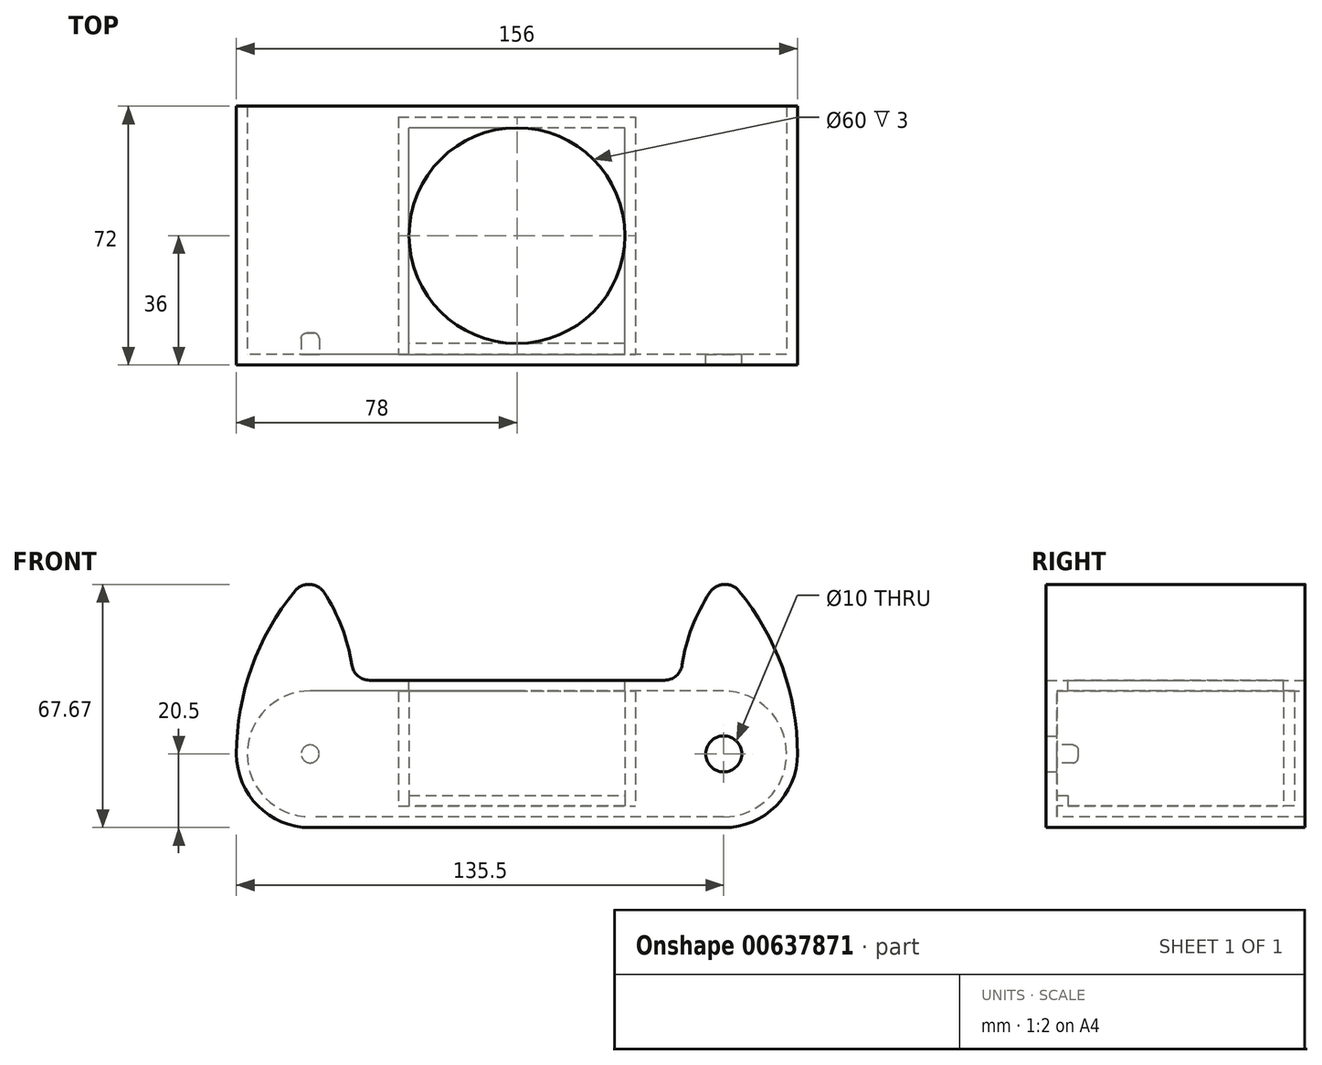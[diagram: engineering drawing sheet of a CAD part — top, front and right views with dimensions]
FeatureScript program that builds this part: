
annotation { "Feature Type Name" : "Feature", "Feature Type Description" : "" }
export const myFeature = defineFeature(function(context is Context, id is Id, definition is map)
    precondition{}
    {
        {
            var Q0;
            Q0=qCreatedBy(makeId("Front.planeOp"),FACE);
            var sketch = newSketch(context, id + "F0", { "sketchPlane" : qUnion([Q0])});
            skLineSegment(sketch, "E0.bottom", {"start": v(57.5, 17.5) * mm, "end": v(-57.5, 17.5) * mm});
            skLineSegment(sketch, "E0.top", {"start": v(57.5, -17.5) * mm, "end": v(-57.5, -17.5) * mm});
            skPoint(sketch, "E0.middle", {"position": v(0, 0) * mm});
            skArc(sketch, "E1", {"start": v(-57.5, 17.5) * mm, "mid": v(-75, 0) * mm, "end": v(-57.5, -17.5) * mm});
            skArc(sketch, "E2", {"start": v(57.5, -17.5) * mm, "mid": v(75, 0) * mm, "end": v(57.5, 17.5) * mm});
            skCircle(sketch, "E3", {"center": v(57.5, 0) * mm, "radius": 5 * mm});
            skSolve(sketch);
        }
        {
            var Q0;
            Q0 = qSketchRegion(id + "F0", true);
            extrude(context, id + "F1", {"entities" : qUnion([Q0]), "depth" : 3 * mm, "offsetDistance" : 25 * mm});
        }
        {
            var Q0;
            Q0=makeQuery(id+"F1.opExtrude","CAP_FACE",FACE,{"disambiguationData":[OSD([sQuery(id+"F0.wireOp",EDGE,"E0.bottom"),sQuery(id+"F0.wireOp",EDGE,"E0.top"),sQuery(id+"F0.wireOp",EDGE,"E1"),sQuery(id+"F0.wireOp",EDGE,"E2"),sQuery(id+"F0.wireOp",EDGE,"E3")])],"isStart":true});
            var sketch = newSketch(context, id + "F2", { "sketchPlane" : qUnion([Q0])});
            skLineSegment(sketch, "E4.bottom", {"start": v(33, -11.5) * mm, "end": v(-33, -11.5) * mm});
            skLineSegment(sketch, "E4.top", {"start": v(33, -14.5) * mm, "end": v(-33, -14.5) * mm});
            skLineSegment(sketch, "E4.left", {"start": v(33, -11.5) * mm, "end": v(33, -14.5) * mm});
            skLineSegment(sketch, "E4.right", {"start": v(-33, -11.5) * mm, "end": v(-33, -14.5) * mm});
            skPoint(sketch, "E4.middle", {"position": v(0, -13) * mm});
            skSolve(sketch);
        }
        {
            var Q0;
            Q0 = qSketchRegion(id + "F2", true);
            extrude(context, id + "F3", {"entities" : qUnion([Q0]), "operationType" : NewBodyOperationType.ADD, "depth" : 66 * mm, "offsetDistance" : 25 * mm});
        }
        {
            var Q0;
            Q0=makeQuery(id+"F3.opExtrude","SWEPT_FACE",FACE,{"disambiguationData":[OSD([sQuery(id+"F2.wireOp",EDGE,"E4.top")])]});
            var sketch = newSketch(context, id + "F4", { "sketchPlane" : qUnion([Q0])});
            skLineSegment(sketch, "E5", {"start": v(0, 0) * mm, "end": v(0, -66) * mm, "construction": true});
            skLineSegment(sketch, "E6.bottom", {"start": v(30, -3) * mm, "end": v(-30, -3) * mm});
            skLineSegment(sketch, "E6.top", {"start": v(30, -63) * mm, "end": v(-30, -63) * mm});
            skLineSegment(sketch, "E6.left", {"start": v(30, -3) * mm, "end": v(30, -63) * mm});
            skLineSegment(sketch, "E6.right", {"start": v(-30, -3) * mm, "end": v(-30, -63) * mm});
            skPoint(sketch, "E6.middle", {"position": v(0, -33) * mm});
            skSolve(sketch);
        }
        {
            var Q0;
            Q0 = qSketchRegion(id + "F4", true);
            extrude(context, id + "F5", {"entities" : qUnion([Q0]), "operationType" : NewBodyOperationType.REMOVE, "oppositeDirection" : true, "depth" : 25 * mm, "offsetDistance" : 25 * mm});
        }
        {
            var Q0;
            Q0=makeQuery(id+"F1.opExtrude","CAP_FACE",FACE,{"disambiguationData":[OSD([sQuery(id+"F0.wireOp",EDGE,"E0.bottom"),sQuery(id+"F0.wireOp",EDGE,"E0.top"),sQuery(id+"F0.wireOp",EDGE,"E1"),sQuery(id+"F0.wireOp",EDGE,"E2"),sQuery(id+"F0.wireOp",EDGE,"E3")])],"isStart":true});
            var sketch = newSketch(context, id + "F6", { "sketchPlane" : qUnion([Q0])});
            skLineSegment(sketch, "E7", {"start": v(57.5, 17.5) * mm, "end": v(57.5, -17.5) * mm, "construction": true});
            skCircle(sketch, "E8", {"center": v(57.5, 0) * mm, "radius": 2.5 * mm});
            skSolve(sketch);
        }
        {
            var Q0;
            Q0 = qSketchRegion(id + "F6", true);
            extrude(context, id + "F7", {"entities" : qUnion([Q0]), "operationType" : NewBodyOperationType.ADD, "depth" : 5.9 * mm, "offsetDistance" : 25 * mm});
        }
        {
            var Q0;
            Q0=makeQuery(id+"F7.opExtrude","CAP_EDGE",EDGE,{"disambiguationData":[OSD([sQuery(id+"F6.wireOp",EDGE,"E8")])],"isStart":false});
            fillet(context, id + "F8", {"entities" : qUnion([Q0]), "radius" : 1.5 * mm, "tangentPropagation" : true, "allowEdgeOverflow" : false});
        }
        {
            var Q0;
            Q0=makeQuery(id+"F1.opExtrude","CAP_FACE",FACE,{"disambiguationData":[OSD([sQuery(id+"F0.wireOp",EDGE,"E0.bottom"),sQuery(id+"F0.wireOp",EDGE,"E0.top"),sQuery(id+"F0.wireOp",EDGE,"E1"),sQuery(id+"F0.wireOp",EDGE,"E2"),sQuery(id+"F0.wireOp",EDGE,"E3")])],"isStart":true});
            var sketch = newSketch(context, id + "F9", { "sketchPlane" : qUnion([Q0])});
            skLineSegment(sketch, "E9", {"start": v(75, 0) * mm, "end": v(78, 0) * mm});
            skLineSegment(sketch, "E10", {"start": v(-75, 0) * mm, "end": v(-78, 0) * mm});
            skLineSegment(sketch, "E11", {"start": v(-57.5, -17.5) * mm, "end": v(-57.5, -20.5) * mm});
            skLineSegment(sketch, "E12", {"start": v(57.5, -17.5) * mm, "end": v(57.5, -20.5) * mm});
            skArc(sketch, "E13", {"start": v(-75, 0) * mm, "mid": v(-69.87, -12.37) * mm, "end": v(-57.5, -17.5) * mm});
            skArc(sketch, "E14", {"start": v(57.5, -17.5) * mm, "mid": v(69.87, -12.37) * mm, "end": v(75, 0) * mm});
            skArc(sketch, "E15", {"start": v(57.5, -20.5) * mm, "mid": v(72, -14.5) * mm, "end": v(78, 0) * mm});
            skArc(sketch, "E16", {"start": v(-78, 0) * mm, "mid": v(-72, -14.5) * mm, "end": v(-57.5, -20.5) * mm});
            skLineSegment(sketch, "E17", {"start": v(-57.5, -20.5) * mm, "end": v(57.5, -20.5) * mm});
            skLineSegment(sketch, "E18", {"start": v(57.5, -17.5) * mm, "end": v(-57.5, -17.5) * mm});
            skSolve(sketch);
        }
        {
            var Q0;
            Q0 = qSketchRegion(id + "F9", true);
            extrude(context, id + "F10", {"entities" : qUnion([Q0]), "operationType" : NewBodyOperationType.ADD, "depth" : 69 * mm, "offsetDistance" : 25 * mm, "hasSecondDirection" : true, "secondDirectionOppositeDirection" : true, "secondDirectionDepth" : 3 * mm});
        }
        {
            var Q0;
            Q0=makeQuery(id+"F3.opExtrude","SWEPT_FACE",FACE,{"disambiguationData":[OSD([sQuery(id+"F2.wireOp",EDGE,"E4.bottom")])]});
            var sketch = newSketch(context, id + "F11", { "sketchPlane" : qUnion([Q0])});
            skLineSegment(sketch, "E19.bottom", {"start": v(-33, 66) * mm, "end": v(33, 66) * mm});
            skLineSegment(sketch, "E19.top", {"start": v(-33, 63) * mm, "end": v(33, 63) * mm});
            skLineSegment(sketch, "E19.left", {"start": v(-33, 66) * mm, "end": v(-33, 63) * mm});
            skLineSegment(sketch, "E19.right", {"start": v(33, 66) * mm, "end": v(33, 63) * mm});
            skSolve(sketch);
        }
        {
            var Q0;
            Q0 = qSketchRegion(id + "F11", true);
            extrude(context, id + "F12", {"entities" : qUnion([Q0]), "operationType" : NewBodyOperationType.ADD, "depth" : 29 * mm, "offsetDistance" : 25 * mm});
        }
        {
            var Q0;
            Q0=makeQuery(id+"F3.opExtrude","SWEPT_FACE",FACE,{"disambiguationData":[OSD([sQuery(id+"F2.wireOp",EDGE,"E4.bottom")])]});
            var sketch = newSketch(context, id + "F13", { "sketchPlane" : qUnion([Q0])});
            skLineSegment(sketch, "E20.bottom", {"start": v(-33, 0) * mm, "end": v(-30, 0) * mm});
            skLineSegment(sketch, "E20.top", {"start": v(-33, 63) * mm, "end": v(-30, 63) * mm});
            skLineSegment(sketch, "E20.left", {"start": v(-33, 0) * mm, "end": v(-33, 63) * mm});
            skLineSegment(sketch, "E20.right", {"start": v(-30, 0) * mm, "end": v(-30, 63) * mm});
            skLineSegment(sketch, "E21.bottom", {"start": v(33, 0) * mm, "end": v(30, 0) * mm});
            skLineSegment(sketch, "E21.top", {"start": v(33, 63) * mm, "end": v(30, 63) * mm});
            skLineSegment(sketch, "E21.left", {"start": v(33, 0) * mm, "end": v(33, 63) * mm});
            skLineSegment(sketch, "E21.right", {"start": v(30, 0) * mm, "end": v(30, 63) * mm});
            skSolve(sketch);
        }
        {
            var Q0;
            Q0 = qSketchRegion(id + "F13", true);
            extrude(context, id + "F14", {"entities" : qUnion([Q0]), "operationType" : NewBodyOperationType.ADD, "depth" : 29 * mm, "offsetDistance" : 25 * mm});
        }
        {
            var Q0;
            Q0=makeQuery(id+"F10.opExtrude","CAP_FACE",FACE,{"disambiguationData":[OSD([sQuery(id+"F9.wireOp",EDGE,"E9"),sQuery(id+"F9.wireOp",EDGE,"E10"),sQuery(id+"F9.wireOp",EDGE,"E13"),sQuery(id+"F9.wireOp",EDGE,"E14"),sQuery(id+"F9.wireOp",EDGE,"E15"),sQuery(id+"F9.wireOp",EDGE,"E16"),sQuery(id+"F9.wireOp",EDGE,"E17"),sQuery(id+"F9.wireOp",EDGE,"E18")])],"isStart":false});
            var sketch = newSketch(context, id + "F15", { "sketchPlane" : qUnion([Q0])});
            skLineSegment(sketch, "E22.bottom", {"start": v(57.5, 17.5) * mm, "end": v(-57.5, 17.5) * mm, "construction": true});
            skLineSegment(sketch, "E22.top", {"start": v(57.5, 17.5) * mm, "end": v(-57.5, 17.5) * mm, "construction": true});
            skLineSegment(sketch, "E22.left", {"start": v(57.5, 17.5) * mm, "end": v(57.5, 17.5) * mm});
            skLineSegment(sketch, "E22.right", {"start": v(-57.5, 17.5) * mm, "end": v(-57.5, 17.5) * mm});
            skPoint(sketch, "E22.middle", {"position": v(0, 17.5) * mm});
            skArc(sketch, "E23", {"start": v(-57.5, 17.5) * mm, "mid": v(-69.87, 12.37) * mm, "end": v(-75, 0) * mm});
            skArc(sketch, "E24", {"start": v(75, 0) * mm, "mid": v(69.87, 12.37) * mm, "end": v(57.5, 17.5) * mm});
            skLineSegment(sketch, "E25", {"start": v(-57.5, 17.5) * mm, "end": v(57.5, 17.5) * mm});
            skLineSegment(sketch, "E26.bottom", {"start": v(-78, 0) * mm, "end": v(-45.5, 0) * mm, "construction": true});
            skLineSegment(sketch, "E26.top", {"start": v(-78, 50) * mm, "end": v(-45.5, 50) * mm, "construction": true});
            skLineSegment(sketch, "E26.left", {"start": v(-78, 0) * mm, "end": v(-78, 50) * mm, "construction": true});
            skLineSegment(sketch, "E26.right", {"start": v(-45.5, 0) * mm, "end": v(-45.5, 50) * mm, "construction": true});
            skLineSegment(sketch, "E27.bottom", {"start": v(78, 0) * mm, "end": v(45.5, 0) * mm, "construction": true});
            skLineSegment(sketch, "E27.top", {"start": v(78, 50) * mm, "end": v(45.5, 50) * mm, "construction": true});
            skLineSegment(sketch, "E27.left", {"start": v(78, 0) * mm, "end": v(78, 50) * mm, "construction": true});
            skLineSegment(sketch, "E27.right", {"start": v(45.5, 0) * mm, "end": v(45.5, 50) * mm, "construction": true});
            skLineSegment(sketch, "E28", {"start": v(-45.5, 20.5) * mm, "end": v(45.5, 20.5) * mm});
            skPoint(sketch, "E28.endSnap0", {"position": v(45.5, 25) * mm});
            skArc(sketch, "E29", {"start": v(-57.5, 50) * mm, "mid": v(-72.68, 27.02) * mm, "end": v(-78, 0) * mm});
            skArc(sketch, "E30", {"start": v(-45.5, 20.5) * mm, "mid": v(-49.09, 36.23) * mm, "end": v(-57.5, 50) * mm});
            skArc(sketch, "E31", {"start": v(78, 0) * mm, "mid": v(72.68, 27.02) * mm, "end": v(57.5, 50) * mm});
            skArc(sketch, "E32", {"start": v(57.5, 50) * mm, "mid": v(49.09, 36.23) * mm, "end": v(45.5, 20.5) * mm});
            skLineSegment(sketch, "E33", {"start": v(78, 0) * mm, "end": v(75, 0) * mm});
            skLineSegment(sketch, "E34", {"start": v(-75, 0) * mm, "end": v(-78, 0) * mm});
            skSolve(sketch);
        }
        {
            var Q0;
            Q0 = qSketchRegion(id + "F15", true);
            extrude(context, id + "F16", {"entities" : qUnion([Q0]), "operationType" : NewBodyOperationType.ADD, "oppositeDirection" : true, "depth" : 72 * mm, "offsetDistance" : 25 * mm});
        }
        {
            var Q0;
            Q0=makeQuery(id+"F16.opExtrude","SWEPT_EDGE",EDGE,{"disambiguationData":[OSD([sQuery(id+"F15.wireOp",EDGE,"E29"),sQuery(id+"F15.wireOp",EDGE,"E30")])]});
            var Q1;
            Q1=makeQuery(id+"F16.opExtrude","SWEPT_EDGE",EDGE,{"disambiguationData":[OSD([sQuery(id+"F15.wireOp",EDGE,"E31"),sQuery(id+"F15.wireOp",EDGE,"E32")])]});
            var Q2;
            Q2=makeQuery(id+"F16.opExtrude","SWEPT_EDGE",EDGE,{"disambiguationData":[OSD([sQuery(id+"F15.wireOp",EDGE,"E28"),sQuery(id+"F15.wireOp",EDGE,"E32")])]});
            var Q3;
            Q3=makeQuery(id+"F16.opExtrude","SWEPT_EDGE",EDGE,{"disambiguationData":[OSD([sQuery(id+"F15.wireOp",EDGE,"E28"),sQuery(id+"F15.wireOp",EDGE,"E30")])]});
            fillet(context, id + "F17", {"entities" : qUnion([Q0, Q1, Q2, Q3]), "radius" : 5 * mm, "tangentPropagation" : true, "allowEdgeOverflow" : false});
        }
        {
            var Q0;
            Q0=makeQuery(id+"F16.opExtrude","SWEPT_FACE",FACE,{"disambiguationData":[OSD([sQuery(id+"F15.wireOp",EDGE,"E28")])]});
            var sketch = newSketch(context, id + "F18", { "sketchPlane" : qUnion([Q0])});
            skLineSegment(sketch, "E35", {"start": v(0, 69) * mm, "end": v(0, -3) * mm, "construction": true});
            skCircle(sketch, "E36", {"center": v(0, 33) * mm, "radius": 30 * mm});
            skSolve(sketch);
        }
        {
            var Q0;
            Q0 = qSketchRegion(id + "F18", true);
            extrude(context, id + "F19", {"entities" : qUnion([Q0]), "operationType" : NewBodyOperationType.REMOVE, "oppositeDirection" : true, "depth" : 25 * mm, "offsetDistance" : 25 * mm});
        }
    });
